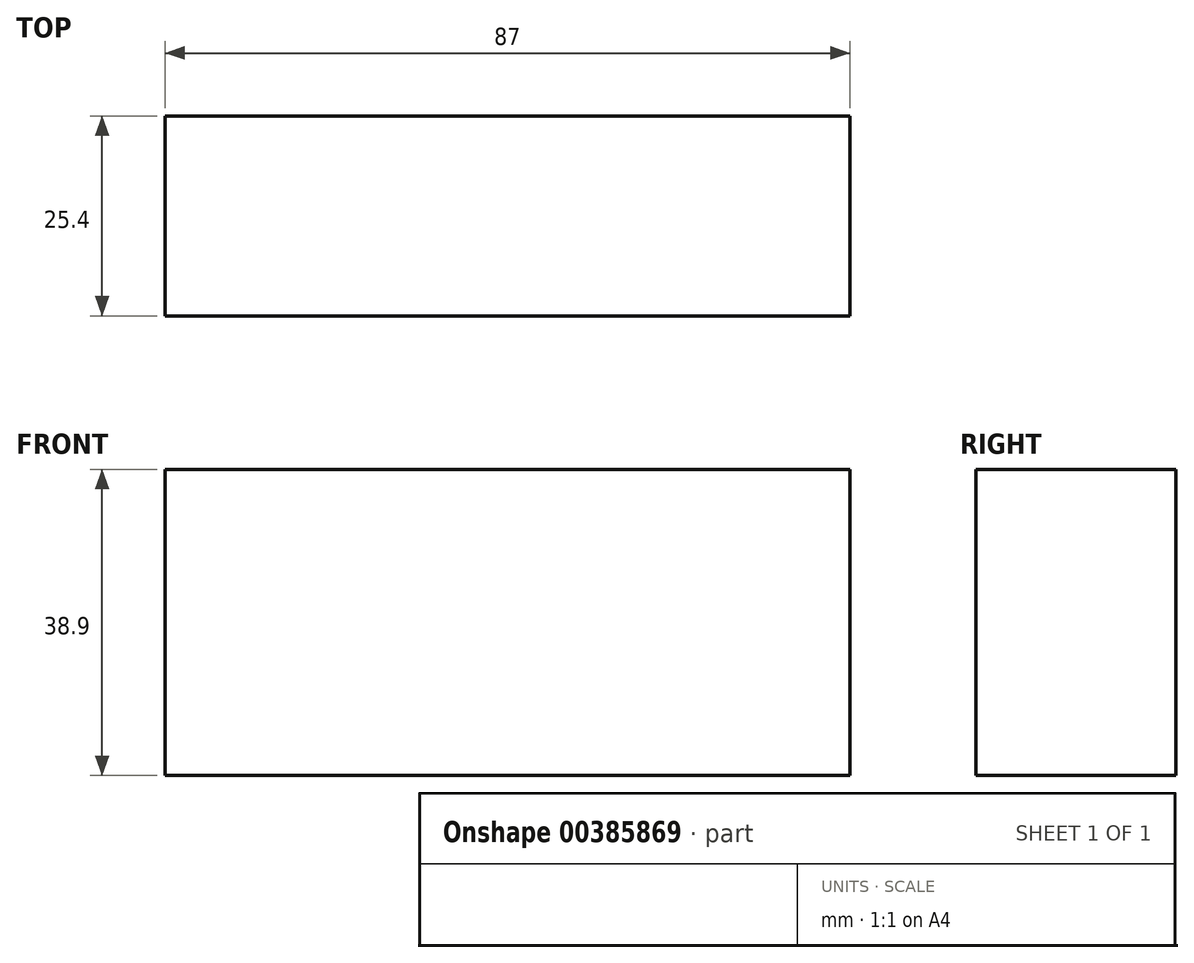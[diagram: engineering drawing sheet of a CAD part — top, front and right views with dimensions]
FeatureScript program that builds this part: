
annotation { "Feature Type Name" : "Feature", "Feature Type Description" : "" }
export const myFeature = defineFeature(function(context is Context, id is Id, definition is map)
    precondition{}
    {
        {
            var Q0;
            Q0=qCreatedBy(makeId("Front.planeOp"),FACE);
            var sketch = newSketch(context, id + "F0", { "sketchPlane" : qUnion([Q0])});
            skLineSegment(sketch, "E0.bottom", {"start": v(-52.89, -8.45) * mm, "end": v(34.11, -8.45) * mm});
            skLineSegment(sketch, "E0.top", {"start": v(-52.89, 30.45) * mm, "end": v(34.11, 30.45) * mm});
            skLineSegment(sketch, "E0.left", {"start": v(-52.89, -8.45) * mm, "end": v(-52.89, 30.45) * mm});
            skLineSegment(sketch, "E0.right", {"start": v(34.11, -8.45) * mm, "end": v(34.11, 30.45) * mm});
            skSolve(sketch);
        }
        {
            var Q0;
            Q0 = qSketchRegion(id + "F0", true);
            extrude(context, id + "F1", {"entities" : qUnion([Q0]), "depth" : 25.4 * mm});
        }
    });
